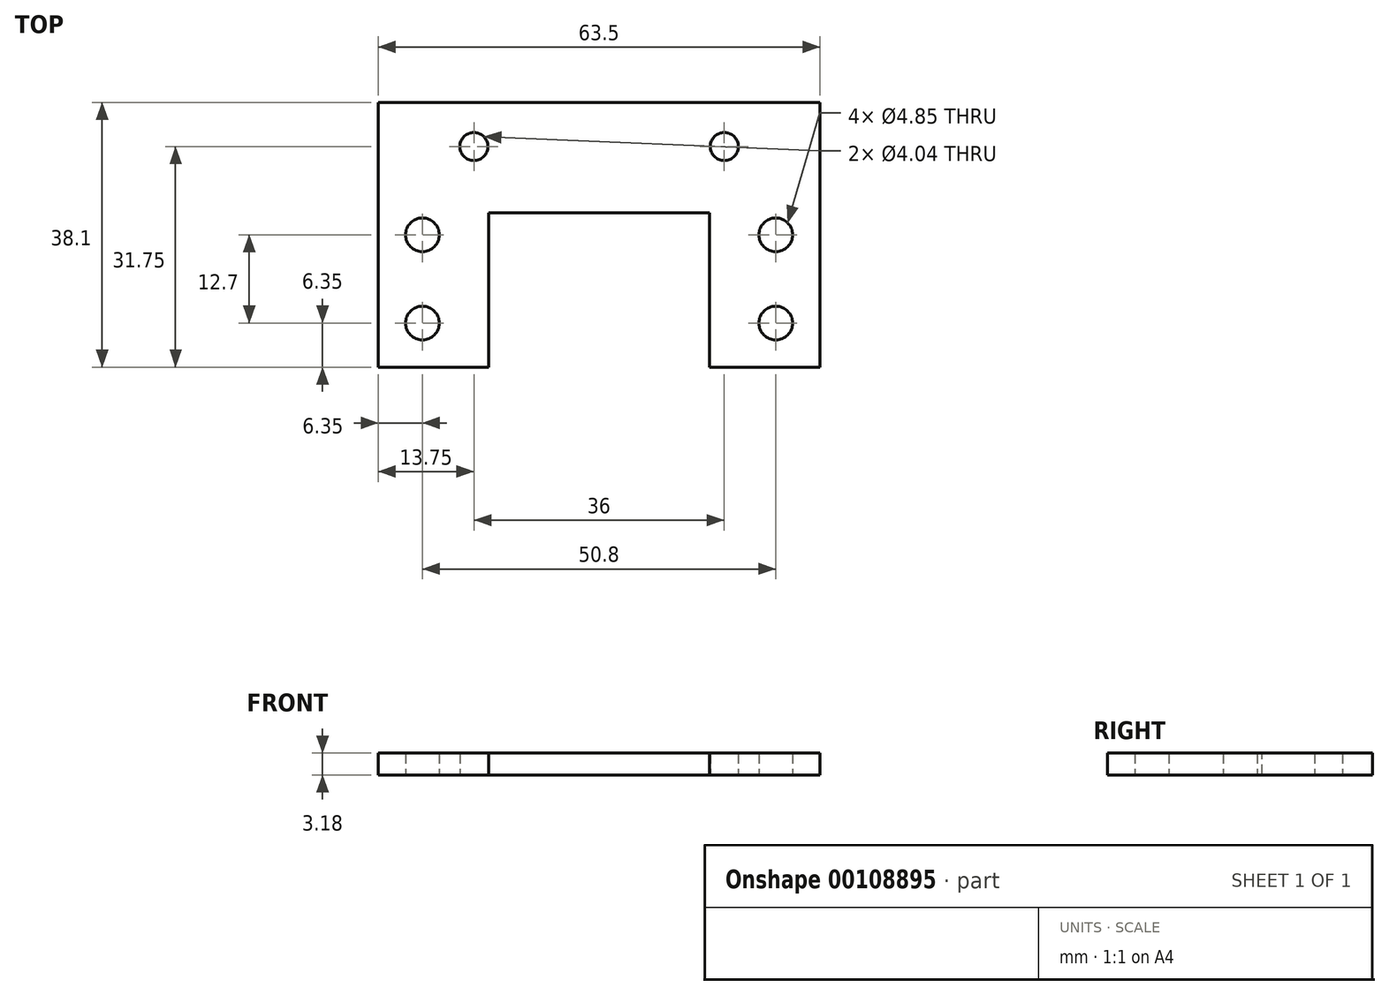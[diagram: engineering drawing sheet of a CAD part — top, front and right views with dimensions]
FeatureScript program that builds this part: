
annotation { "Feature Type Name" : "Feature", "Feature Type Description" : "" }
export const myFeature = defineFeature(function(context is Context, id is Id, definition is map)
    precondition{}
    {
        {
            var Q0;
            Q0=qCreatedBy(makeId("Top.planeOp"),FACE);
            var sketch = newSketch(context, id + "F0", { "sketchPlane" : qUnion([Q0])});
            skLineSegment(sketch, "E0.bottom", {"start": v(31.75, 19.05) * mm, "end": v(-31.75, 19.05) * mm});
            skLineSegment(sketch, "E0.top", {"start": v(31.75, -19.05) * mm, "end": v(-31.75, -19.05) * mm});
            skLineSegment(sketch, "E0.left", {"start": v(31.75, 19.05) * mm, "end": v(31.75, -19.05) * mm});
            skLineSegment(sketch, "E0.right", {"start": v(-31.75, 19.05) * mm, "end": v(-31.75, -19.05) * mm});
            skPoint(sketch, "E0.middle", {"position": v(0, 0) * mm});
            skCircle(sketch, "E1", {"center": v(-25.4, -12.7) * mm, "radius": 2.43 * mm});
            skCircle(sketch, "E2", {"center": v(-25.4, 0) * mm, "radius": 2.43 * mm});
            skCircle(sketch, "E3.MirrorC", {"center": v(25.4, 0) * mm, "radius": 2.43 * mm});
            skCircle(sketch, "E4.MirrorC", {"center": v(25.4, -12.7) * mm, "radius": 2.43 * mm});
            skCircle(sketch, "E5", {"center": v(-18, 12.7) * mm, "radius": 2.02 * mm});
            skCircle(sketch, "E6.MirrorC", {"center": v(18, 12.7) * mm, "radius": 2.02 * mm});
            skSolve(sketch);
        }
        {
            var Q0;
            Q0 = qSketchRegion(id + "F0", true);
            extrude(context, id + "F1", {"entities" : qUnion([Q0]), "depth" : 3.17 * mm});
        }
        {
            var Q0;
            Q0=makeQuery(id+"F1.opExtrude","CAP_FACE",FACE,{"disambiguationData":[OSD([sQuery(id+"F0.wireOp",EDGE,"E0.bottom"),sQuery(id+"F0.wireOp",EDGE,"E0.top"),sQuery(id+"F0.wireOp",EDGE,"E0.left"),sQuery(id+"F0.wireOp",EDGE,"E0.right"),sQuery(id+"F0.wireOp",EDGE,"E1"),sQuery(id+"F0.wireOp",EDGE,"E2"),sQuery(id+"F0.wireOp",EDGE,"E3.MirrorC"),sQuery(id+"F0.wireOp",EDGE,"E4.MirrorC"),sQuery(id+"F0.wireOp",EDGE,"E5"),sQuery(id+"F0.wireOp",EDGE,"E6.MirrorC")])],"isStart":false});
            var sketch = newSketch(context, id + "F2", { "sketchPlane" : qUnion([Q0])});
            skLineSegment(sketch, "E7", {"start": v(-15.88, -19.05) * mm, "end": v(-15.88, 3.18) * mm});
            skLineSegment(sketch, "E8", {"start": v(-15.88, 3.18) * mm, "end": v(15.88, 3.18) * mm});
            skLineSegment(sketch, "E9", {"start": v(15.87, 3.18) * mm, "end": v(15.88, -19.05) * mm});
            skLineSegment(sketch, "E10", {"start": v(-15.88, -19.05) * mm, "end": v(15.88, -19.05) * mm});
            skSolve(sketch);
        }
        {
            var Q0;
            Q0 = qSketchRegion(id + "F2", true);
            extrude(context, id + "F3", {"entities" : qUnion([Q0]), "operationType" : NewBodyOperationType.REMOVE, "endBound" : BoundingType.THROUGH_ALL, "oppositeDirection" : true, "depth" : 25.4 * mm});
        }
    });
